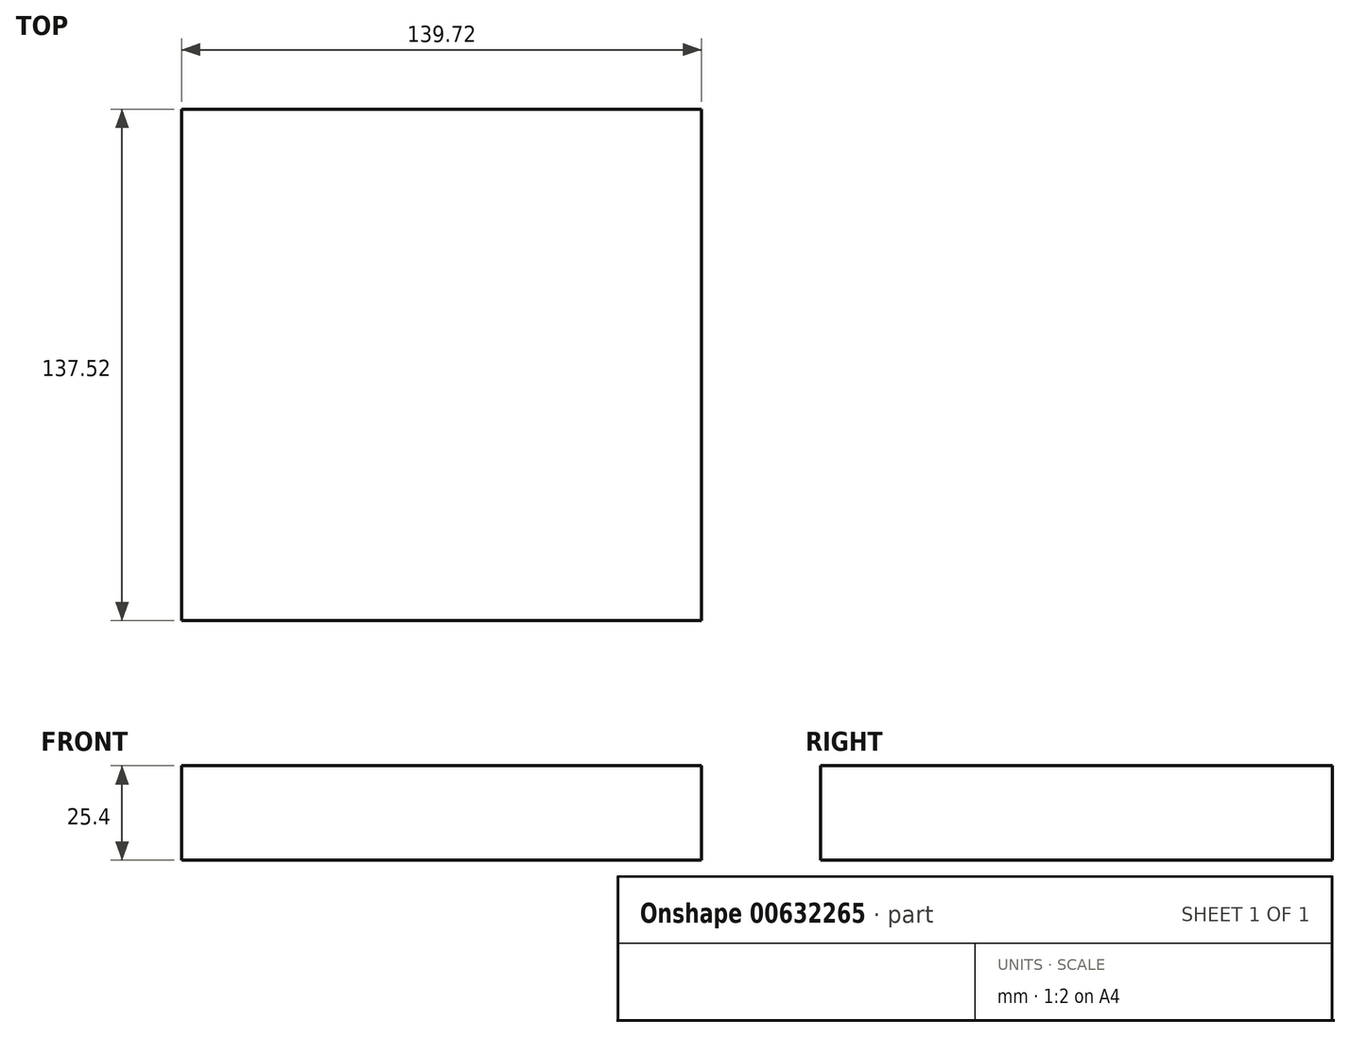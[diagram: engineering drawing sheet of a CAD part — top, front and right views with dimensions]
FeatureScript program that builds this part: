
annotation { "Feature Type Name" : "Feature", "Feature Type Description" : "" }
export const myFeature = defineFeature(function(context is Context, id is Id, definition is map)
    precondition{}
    {
        {
            var Q0;
            Q0=qCreatedBy(makeId("Top.planeOp"),FACE);
            var sketch = newSketch(context, id + "F0", { "sketchPlane" : qUnion([Q0])});
            skLineSegment(sketch, "E0.bottom", {"start": v(69.86, -68.76) * mm, "end": v(-69.86, -68.76) * mm});
            skLineSegment(sketch, "E0.top", {"start": v(69.86, 68.76) * mm, "end": v(-69.86, 68.76) * mm});
            skLineSegment(sketch, "E0.left", {"start": v(69.86, -68.76) * mm, "end": v(69.86, 68.76) * mm});
            skLineSegment(sketch, "E0.right", {"start": v(-69.86, -68.76) * mm, "end": v(-69.86, 68.76) * mm});
            skPoint(sketch, "E0.middle", {"position": v(0, 0) * mm});
            skLineSegment(sketch, "E1", {"start": v(0, 68.76) * mm, "end": v(0, -68.76) * mm});
            skSolve(sketch);
        }
        {
            var Q0;
            {var subQ0=sQuery(id+"F0.wireOp",EDGE,"E0.left");Q0=makeQuery(id+"F0.imprint","IMPRINT",FACE,{"disambiguationData":[TD([[makeQuery(id+"F0.imprint","IMPRINT",EDGE,{"derivedFrom":subQ0}),1.0]])]});}
            extrude(context, id + "F1", {"entities" : qUnion([Q0]), "depth" : 25.4 * mm, "offsetDistance" : 25.4 * mm});
        }
        {
            var Q0;
            {var subQ0=sQuery(id+"F0.wireOp",EDGE,"E0.right");Q0=makeQuery(id+"F0.imprint","IMPRINT",FACE,{"disambiguationData":[TD([[makeQuery(id+"F0.imprint","IMPRINT",EDGE,{"derivedFrom":subQ0}),-1.0]])]});}
            extrude(context, id + "F2", {"entities" : qUnion([Q0]), "operationType" : NewBodyOperationType.ADD, "depth" : 25.4 * mm, "offsetDistance" : 25.4 * mm});
        }
    });
